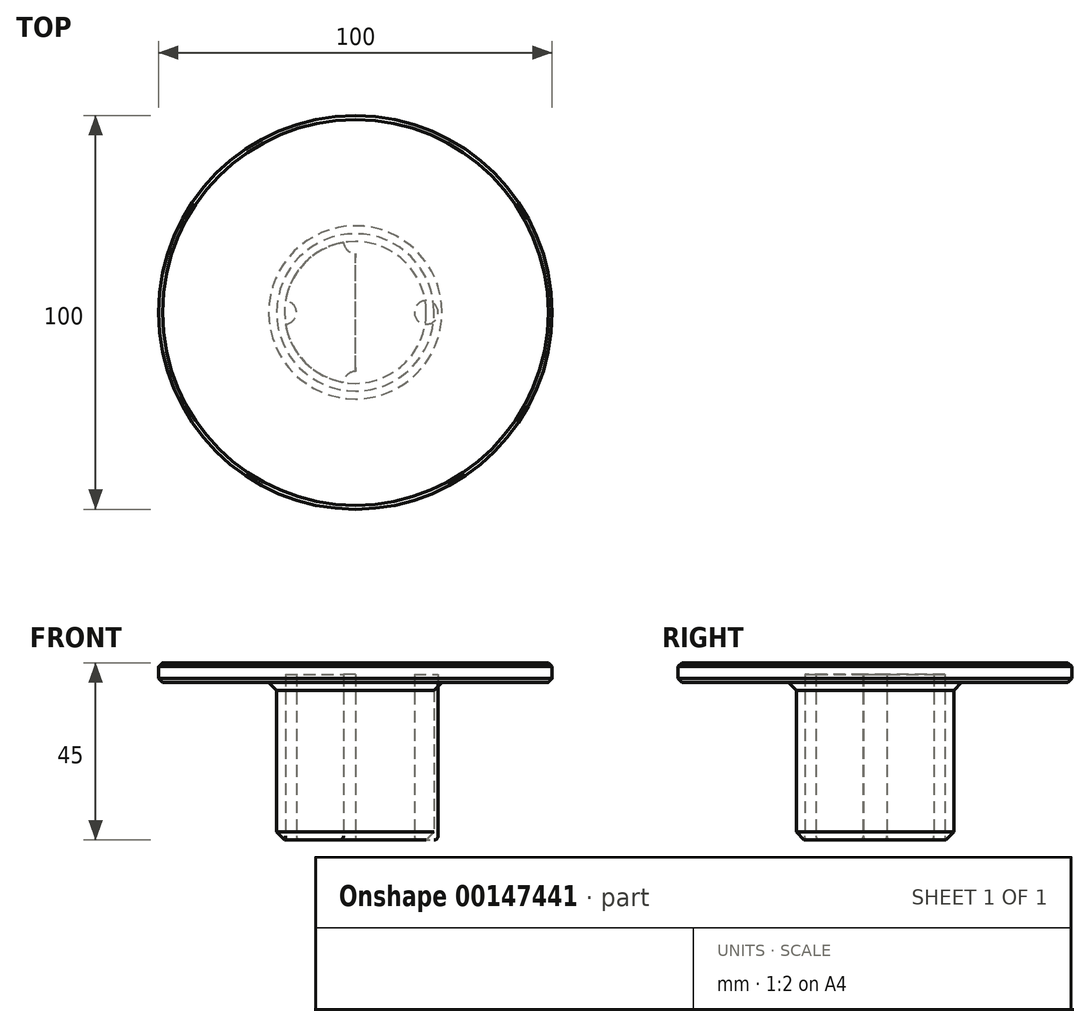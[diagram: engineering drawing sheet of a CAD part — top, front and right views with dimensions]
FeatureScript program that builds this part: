
annotation { "Feature Type Name" : "Feature", "Feature Type Description" : "" }
export const myFeature = defineFeature(function(context is Context, id is Id, definition is map)
    precondition{}
    {
        {
            var Q0;
            Q0=qCreatedBy(makeId("Front.planeOp"),FACE);
            var sketch = newSketch(context, id + "F0", { "sketchPlane" : qUnion([Q0])});
            skLineSegment(sketch, "E0", {"start": v(0, 0) * mm, "end": v(-50, 0) * mm});
            skLineSegment(sketch, "E1", {"start": v(-50, 0) * mm, "end": v(-50, -5) * mm});
            skLineSegment(sketch, "E2", {"start": v(-50, -5) * mm, "end": v(-20, -5) * mm});
            skLineSegment(sketch, "E3", {"start": v(-20, -5) * mm, "end": v(-20, -45) * mm});
            skLineSegment(sketch, "E4", {"start": v(-20, -45) * mm, "end": v(0, -45) * mm});
            skLineSegment(sketch, "E5", {"start": v(0, -45) * mm, "end": v(0, 0) * mm});
            skSolve(sketch);
        }
        {
            var Q0;
            Q0=makeQuery(id+"F0.imprint","IMPRINT",FACE,{"disambiguationData":[TD([[makeQuery(id+"F0.imprint","IMPRINT",EDGE,{"derivedFrom":sQuery(id+"F0.wireOp",EDGE,"E0")}),1.0]])]});
            var Q1;
            Q1=sQuery(id+"F0.wireOp",EDGE,"E5");
            revolve(context, id + "F1", {"entities" : qUnion([Q0]), "axis" : qUnion([Q1]), "revolveType" : RevolveType.FULL});
        }
        {
            var Q0;
            Q0=makeQuery(id+"F1.opRevolve","SWEPT_EDGE",EDGE,{"disambiguationData":[OSD([sQuery(id+"F0.wireOp",EDGE,"E3"),sQuery(id+"F0.wireOp",EDGE,"E4")])]});
            var Q1;
            Q1=makeQuery(id+"F1.opRevolve","SWEPT_EDGE",EDGE,{"disambiguationData":[OSD([sQuery(id+"F0.wireOp",EDGE,"E2"),sQuery(id+"F0.wireOp",EDGE,"E3")])]});
            var Q2;
            Q2=makeQuery(id+"F5JyQewPJ2aA4EM_1.opLoft","MID_CAP_EDGE",EDGE,{"disambiguationData":[OSD([sQuery(id+"Fzj4vK8QTupCjVk_1.wireOp",EDGE,"MMnmbx8W-rHfF-ifZP-rguA-HF9lVHHnug6x")])],"capPos":0.0});
            var Q3;
            Q3=makeQuery(id+"FLFetyTCZcl8UhI_1.opLoft","MID_CAP_EDGE",EDGE,{"disambiguationData":[OSD([sQuery(id+"Fzj4vK8QTupCjVk_1.wireOp",EDGE,"bSrS4Rm6-p3bf-OkdZ-sIeg-5JjVo9qfkx47")])],"capPos":0.0});
            var Q4;
            Q4=makeQuery(id+"F5bgLMzHz8UBm4O_1.opLoft","MID_CAP_EDGE",EDGE,{"disambiguationData":[OSD([sQuery(id+"Fzj4vK8QTupCjVk_1.wireOp",EDGE,"XPQSvpZP-MHd5-XJOv-AZr6-iTBv5oSfEAo2"),sQuery(id+"FNucxagRUR8c6Vn_1.wireOp",EDGE,"Sua980v0-691b-DHNz-DGnp-ehrl0rSRF3u3")])],"capPos":1.0});
            var Q5;
            Q5=makeQuery(id+"FImIpoPiMxvuPUx_1.opLoft","MID_CAP_EDGE",EDGE,{"disambiguationData":[OSD([sQuery(id+"Fzj4vK8QTupCjVk_1.wireOp",EDGE,"MH1ERuJN-EFIX-3wg7-KvgR-c01uIAdwXBZZ"),sQuery(id+"FNucxagRUR8c6Vn_1.wireOp",EDGE,"xx9w8jU4-vBEM-m0Wx-UBBP-Oq3wZTKVYH9m")])],"capPos":1.0});
            chamfer(context, id + "F2", {"entities" : qUnion([Q0, Q1, Q2, Q3, Q4, Q5]), "width" : 2 * mm, "tangentPropagation" : true});
        }
        {
            var Q0;
            Q0=makeQuery(id+"F1.opRevolve","SWEPT_EDGE",EDGE,{"disambiguationData":[OSD([sQuery(id+"F0.wireOp",EDGE,"E1"),sQuery(id+"F0.wireOp",EDGE,"E2")])]});
            var Q1;
            Q1=makeQuery(id+"F1.opRevolve","SWEPT_EDGE",EDGE,{"disambiguationData":[OSD([sQuery(id+"F0.wireOp",EDGE,"E0"),sQuery(id+"F0.wireOp",EDGE,"E1")])]});
            var Q2;
            Q2=makeQuery(id+"FImIpoPiMxvuPUx_1.opLoft","MID_CAP_EDGE",EDGE,{"disambiguationData":[OSD([sQuery(id+"FNucxagRUR8c6Vn_1.wireOp",EDGE,"xx9w8jU4-vBEM-m0Wx-UBBP-Oq3wZTKVYH9m")])],"capPos":0.0});
            var Q3;
            Q3=makeQuery(id+"F5bgLMzHz8UBm4O_1.opLoft","MID_CAP_EDGE",EDGE,{"disambiguationData":[OSD([sQuery(id+"FNucxagRUR8c6Vn_1.wireOp",EDGE,"Sua980v0-691b-DHNz-DGnp-ehrl0rSRF3u3")])],"capPos":0.0});
            var Q4;
            Q4=makeQuery(id+"FLFetyTCZcl8UhI_1.opLoft","MID_CAP_EDGE",EDGE,{"disambiguationData":[OSD([sQuery(id+"Fzj4vK8QTupCjVk_1.wireOp",EDGE,"bSrS4Rm6-p3bf-OkdZ-sIeg-5JjVo9qfkx47"),sQuery(id+"FNucxagRUR8c6Vn_1.wireOp",EDGE,"W0ROYUkt-3kAn-Omy5-C3NE-nvRqDPtdsI8T")])],"capPos":1.0});
            var Q5;
            Q5=makeQuery(id+"F5JyQewPJ2aA4EM_1.opLoft","MID_CAP_EDGE",EDGE,{"disambiguationData":[OSD([sQuery(id+"Fzj4vK8QTupCjVk_1.wireOp",EDGE,"MMnmbx8W-rHfF-ifZP-rguA-HF9lVHHnug6x"),sQuery(id+"FNucxagRUR8c6Vn_1.wireOp",EDGE,"xYsWiafD-IE8B-tHJ2-jvhg-KuPzN0yeIyUA")])],"capPos":1.0});
            chamfer(context, id + "F3", {"entities" : qUnion([Q0, Q1, Q2, Q3, Q4, Q5]), "width" : 1 * mm, "tangentPropagation" : true});
        }
        {
            var Q0;
            Q0=makeQuery(id+"F1.opRevolve","SWEPT_FACE",FACE,{"disambiguationData":[OSD([sQuery(id+"F0.wireOp",EDGE,"E4")])]});
            var sketch = newSketch(context, id + "F4", { "sketchPlane" : qUnion([Q0])});
            skLineSegment(sketch, "E6", {"start": v(-41.78, 0) * mm, "end": v(44.48, 0) * mm});
            skLineSegment(sketch, "E7", {"start": v(0, 33.02) * mm, "end": v(0, -34.78) * mm});
            skCircle(sketch, "E8", {"center": v(-18, 0) * mm, "radius": 3 * mm});
            skCircle(sketch, "E9", {"center": v(0, 18) * mm, "radius": 3 * mm});
            skCircle(sketch, "E10.MirrorC", {"center": v(0, -18) * mm, "radius": 3 * mm});
            skLineSegment(sketch, "E11.MirrorCS", {"start": v(0, -33.02) * mm, "end": v(0, 34.78) * mm});
            skCircle(sketch, "E12.MirrorC", {"center": v(18, 0) * mm, "radius": 3 * mm});
            skSolve(sketch);
        }
        {
            var Q0;
            {var subQ0=sQuery(id+"F4.wireOp",EDGE,"E8");var subQ1=sQuery(id+"F4.wireOp",EDGE,"E6");var subQ2=makeQuery(id+"F4.imprint","INTERSECT",VERTEX,{"disambiguationData":[OD(0.0)],"derivedFrom":[subQ1,subQ0]});Q0=makeQuery(id+"F4.imprint","IMPRINT",FACE,{"disambiguationData":[TD([[makeQuery(id+"F4.imprint","IMPRINT",EDGE,{"disambiguationData":[TD([[subQ2,-1.0]])],"derivedFrom":subQ1}),1.0]])]});}
            var Q1;
            {var subQ0=sQuery(id+"F4.wireOp",EDGE,"E8");var subQ1=sQuery(id+"F4.wireOp",EDGE,"E6");var subQ2=makeQuery(id+"F4.imprint","INTERSECT",VERTEX,{"disambiguationData":[OD(0.0)],"derivedFrom":[subQ1,subQ0]});Q1=makeQuery(id+"F4.imprint","IMPRINT",FACE,{"disambiguationData":[TD([[makeQuery(id+"F4.imprint","IMPRINT",EDGE,{"disambiguationData":[TD([[subQ2,-1.0]])],"derivedFrom":subQ1}),-1.0]])]});}
            var Q2;
            {var subQ0=sQuery(id+"F4.wireOp",EDGE,"E11.MirrorCS");var subQ1=sQuery(id+"F4.wireOp",EDGE,"E9");var subQ2=makeQuery(id+"F4.imprint","INTERSECT",VERTEX,{"disambiguationData":[OD(0.0)],"derivedFrom":[subQ1,subQ0]});Q2=makeQuery(id+"F4.imprint","IMPRINT",FACE,{"disambiguationData":[TD([[makeQuery(id+"F4.imprint","IMPRINT",EDGE,{"disambiguationData":[TD([[subQ2,-1.0]])],"derivedFrom":subQ1}),1.0]])]});}
            var Q3;
            {var subQ0=sQuery(id+"F4.wireOp",EDGE,"E11.MirrorCS");var subQ1=sQuery(id+"F4.wireOp",EDGE,"E9");var subQ2=makeQuery(id+"F4.imprint","INTERSECT",VERTEX,{"disambiguationData":[OD(0.0)],"derivedFrom":[subQ1,subQ0]});Q3=makeQuery(id+"F4.imprint","IMPRINT",FACE,{"disambiguationData":[TD([[makeQuery(id+"F4.imprint","IMPRINT",EDGE,{"disambiguationData":[TD([[subQ2,1.0]])],"derivedFrom":subQ1}),1.0]])]});}
            var Q4;
            {var subQ0=sQuery(id+"F4.wireOp",EDGE,"E12.MirrorC");var subQ1=sQuery(id+"F4.wireOp",EDGE,"E6");var subQ2=makeQuery(id+"F4.imprint","INTERSECT",VERTEX,{"disambiguationData":[OD(0.0)],"derivedFrom":[subQ1,subQ0]});Q4=makeQuery(id+"F4.imprint","IMPRINT",FACE,{"disambiguationData":[TD([[makeQuery(id+"F4.imprint","IMPRINT",EDGE,{"disambiguationData":[TD([[subQ2,1.0]])],"derivedFrom":subQ1}),1.0]])]});}
            var Q5;
            {var subQ0=sQuery(id+"F4.wireOp",EDGE,"E12.MirrorC");var subQ1=sQuery(id+"F4.wireOp",EDGE,"E6");var subQ2=makeQuery(id+"F4.imprint","INTERSECT",VERTEX,{"disambiguationData":[OD(0.0)],"derivedFrom":[subQ1,subQ0]});Q5=makeQuery(id+"F4.imprint","IMPRINT",FACE,{"disambiguationData":[TD([[makeQuery(id+"F4.imprint","IMPRINT",EDGE,{"disambiguationData":[TD([[subQ2,1.0]])],"derivedFrom":subQ1}),-1.0]])]});}
            var Q6;
            {var subQ0=sQuery(id+"F4.wireOp",EDGE,"E11.MirrorCS");var subQ1=sQuery(id+"F4.wireOp",EDGE,"E10.MirrorC");var subQ2=makeQuery(id+"F4.imprint","INTERSECT",VERTEX,{"disambiguationData":[OD(1.0)],"derivedFrom":[subQ1,subQ0]});Q6=makeQuery(id+"F4.imprint","IMPRINT",FACE,{"disambiguationData":[TD([[makeQuery(id+"F4.imprint","IMPRINT",EDGE,{"disambiguationData":[TD([[subQ2,-1.0]])],"derivedFrom":subQ1}),-1.0]])]});}
            var Q7;
            {var subQ0=sQuery(id+"F4.wireOp",EDGE,"E11.MirrorCS");var subQ1=sQuery(id+"F4.wireOp",EDGE,"E10.MirrorC");var subQ2=makeQuery(id+"F4.imprint","INTERSECT",VERTEX,{"disambiguationData":[OD(1.0)],"derivedFrom":[subQ1,subQ0]});Q7=makeQuery(id+"F4.imprint","IMPRINT",FACE,{"disambiguationData":[TD([[makeQuery(id+"F4.imprint","IMPRINT",EDGE,{"disambiguationData":[TD([[subQ2,1.0]])],"derivedFrom":subQ1}),-1.0]])]});}
            var Q8;
            {var subQ0=sQuery(id+"F4.wireOp",EDGE,"E11.MirrorCS");var subQ1=sQuery(id+"F4.wireOp",EDGE,"E10.MirrorC");var subQ2=makeQuery(id+"F4.imprint","INTERSECT",VERTEX,{"disambiguationData":[OD(0.0)],"derivedFrom":[subQ1,subQ0]});Q8=makeQuery(id+"F4.imprint","IMPRINT",FACE,{"disambiguationData":[TD([[makeQuery(id+"F4.imprint","IMPRINT",EDGE,{"disambiguationData":[TD([[subQ2,-1.0]])],"derivedFrom":subQ1}),-1.0]])]});}
            var Q9;
            {var subQ0=sQuery(id+"F4.wireOp",EDGE,"E11.MirrorCS");var subQ1=sQuery(id+"F4.wireOp",EDGE,"E10.MirrorC");var subQ2=makeQuery(id+"F4.imprint","INTERSECT",VERTEX,{"disambiguationData":[OD(0.0)],"derivedFrom":[subQ1,subQ0]});Q9=makeQuery(id+"F4.imprint","IMPRINT",FACE,{"disambiguationData":[TD([[makeQuery(id+"F4.imprint","IMPRINT",EDGE,{"disambiguationData":[TD([[subQ2,1.0]])],"derivedFrom":subQ1}),-1.0]])]});}
            var Q10;
            {var subQ0=sQuery(id+"F4.wireOp",EDGE,"E12.MirrorC");var subQ1=sQuery(id+"F4.wireOp",EDGE,"E6");var subQ2=makeQuery(id+"F4.imprint","INTERSECT",VERTEX,{"disambiguationData":[OD(1.0)],"derivedFrom":[subQ1,subQ0]});Q10=makeQuery(id+"F4.imprint","IMPRINT",FACE,{"disambiguationData":[TD([[makeQuery(id+"F4.imprint","IMPRINT",EDGE,{"disambiguationData":[TD([[subQ2,-1.0]])],"derivedFrom":subQ1}),-1.0]])]});}
            var Q11;
            {var subQ0=sQuery(id+"F4.wireOp",EDGE,"E12.MirrorC");var subQ1=sQuery(id+"F4.wireOp",EDGE,"E6");var subQ2=makeQuery(id+"F4.imprint","INTERSECT",VERTEX,{"disambiguationData":[OD(1.0)],"derivedFrom":[subQ1,subQ0]});Q11=makeQuery(id+"F4.imprint","IMPRINT",FACE,{"disambiguationData":[TD([[makeQuery(id+"F4.imprint","IMPRINT",EDGE,{"disambiguationData":[TD([[subQ2,-1.0]])],"derivedFrom":subQ1}),1.0]])]});}
            var Q12;
            {var subQ0=sQuery(id+"F4.wireOp",EDGE,"E11.MirrorCS");var subQ1=sQuery(id+"F4.wireOp",EDGE,"E9");var subQ2=makeQuery(id+"F4.imprint","INTERSECT",VERTEX,{"disambiguationData":[OD(1.0)],"derivedFrom":[subQ1,subQ0]});Q12=makeQuery(id+"F4.imprint","IMPRINT",FACE,{"disambiguationData":[TD([[makeQuery(id+"F4.imprint","IMPRINT",EDGE,{"disambiguationData":[TD([[subQ2,-1.0]])],"derivedFrom":subQ1}),1.0]])]});}
            var Q13;
            {var subQ0=sQuery(id+"F4.wireOp",EDGE,"E11.MirrorCS");var subQ1=sQuery(id+"F4.wireOp",EDGE,"E9");var subQ2=makeQuery(id+"F4.imprint","INTERSECT",VERTEX,{"disambiguationData":[OD(1.0)],"derivedFrom":[subQ1,subQ0]});Q13=makeQuery(id+"F4.imprint","IMPRINT",FACE,{"disambiguationData":[TD([[makeQuery(id+"F4.imprint","IMPRINT",EDGE,{"disambiguationData":[TD([[subQ2,1.0]])],"derivedFrom":subQ1}),1.0]])]});}
            var Q14;
            {var subQ0=sQuery(id+"F4.wireOp",EDGE,"E8");var subQ1=sQuery(id+"F4.wireOp",EDGE,"E6");var subQ2=makeQuery(id+"F4.imprint","INTERSECT",VERTEX,{"disambiguationData":[OD(1.0)],"derivedFrom":[subQ1,subQ0]});Q14=makeQuery(id+"F4.imprint","IMPRINT",FACE,{"disambiguationData":[TD([[makeQuery(id+"F4.imprint","IMPRINT",EDGE,{"disambiguationData":[TD([[subQ2,1.0]])],"derivedFrom":subQ1}),-1.0]])]});}
            var Q15;
            {var subQ0=sQuery(id+"F4.wireOp",EDGE,"E8");var subQ1=sQuery(id+"F4.wireOp",EDGE,"E6");var subQ2=makeQuery(id+"F4.imprint","INTERSECT",VERTEX,{"disambiguationData":[OD(1.0)],"derivedFrom":[subQ1,subQ0]});Q15=makeQuery(id+"F4.imprint","IMPRINT",FACE,{"disambiguationData":[TD([[makeQuery(id+"F4.imprint","IMPRINT",EDGE,{"disambiguationData":[TD([[subQ2,1.0]])],"derivedFrom":subQ1}),1.0]])]});}
            extrude(context, id + "F5", {"entities" : qUnion([Q0, Q1, Q2, Q3, Q4, Q5, Q6, Q7, Q8, Q9, Q10, Q11, Q12, Q13, Q14, Q15]), "oppositeDirection" : true, "depth" : 42 * mm, "offsetDistance" : 25 * mm});
        }
        {
            var Q0;
            Q0=makeQuery(id+"F5.opExtrude","CAP_EDGE",EDGE,{"disambiguationData":[OSD([sQuery(id+"F4.wireOp",EDGE,"E8")])],"isStart":true});
            var Q1;
            Q1=makeQuery(id+"F5.opExtrude","CAP_EDGE",EDGE,{"disambiguationData":[OSD([sQuery(id+"F4.wireOp",EDGE,"E9")])],"isStart":true});
            var Q2;
            Q2=makeQuery(id+"F5.opExtrude","CAP_EDGE",EDGE,{"disambiguationData":[OSD([sQuery(id+"F4.wireOp",EDGE,"E10.MirrorC")])],"isStart":true});
            var Q3;
            Q3=makeQuery(id+"F5.opExtrude","CAP_EDGE",EDGE,{"disambiguationData":[OSD([sQuery(id+"F4.wireOp",EDGE,"E12.MirrorC")])],"isStart":true});
            fillet(context, id + "F6", {"entities" : qUnion([Q0, Q1, Q2, Q3]), "tangentPropagation" : true, "radius" : 1 * mm, "defaultsChanged" : false, "vertexSettings" : [], "allowEdgeOverflow" : false});
        }
    });
